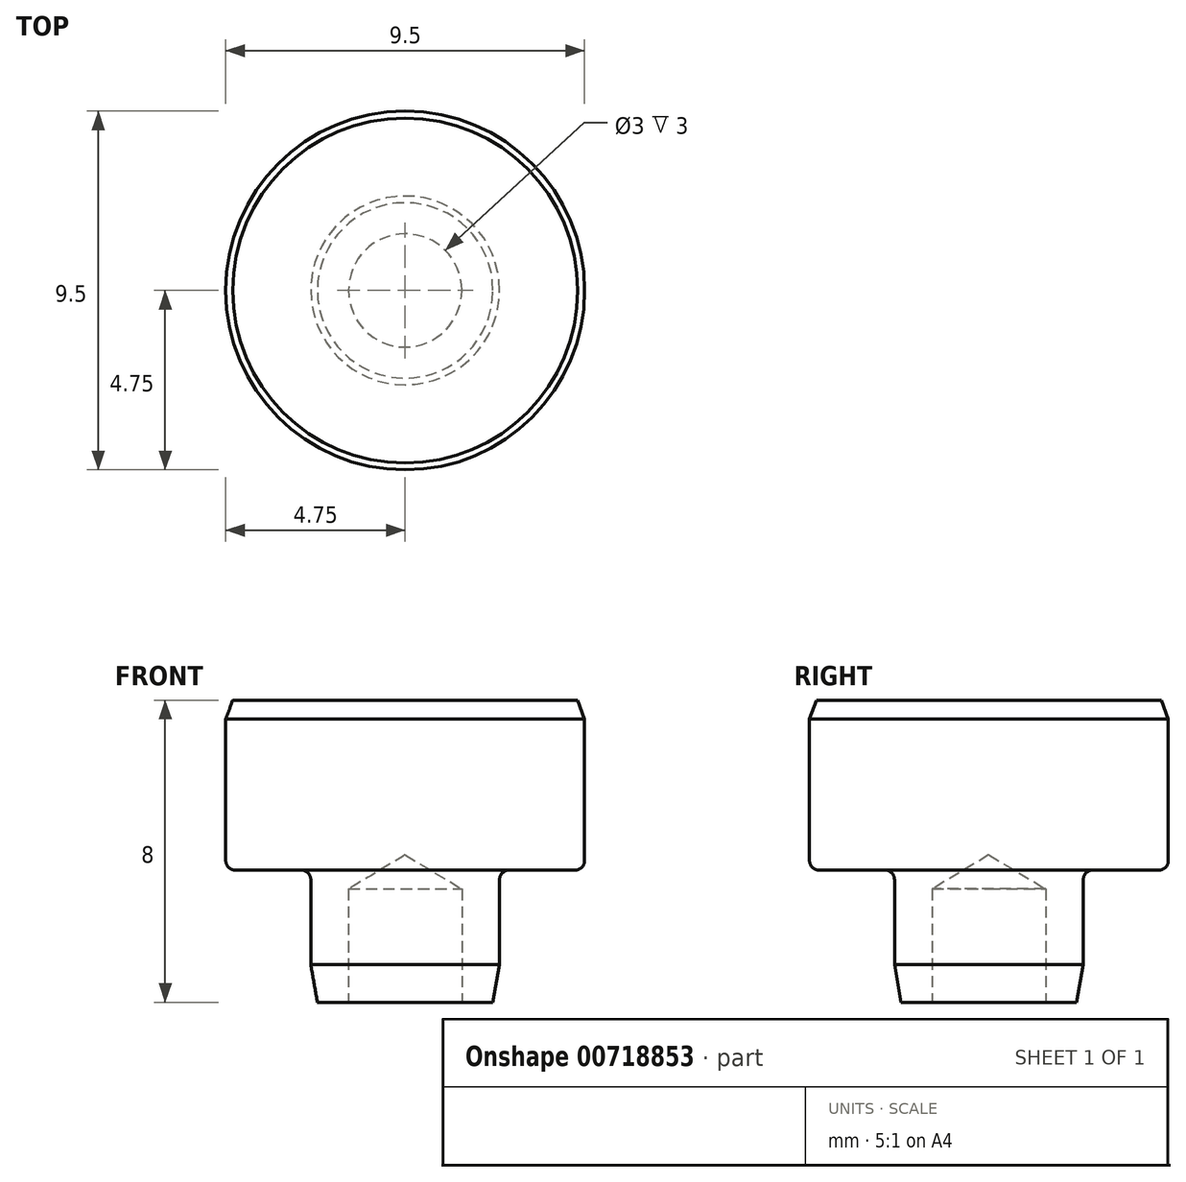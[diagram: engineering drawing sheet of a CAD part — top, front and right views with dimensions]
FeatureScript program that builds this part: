
annotation { "Feature Type Name" : "Feature", "Feature Type Description" : "" }
export const myFeature = defineFeature(function(context is Context, id is Id, definition is map)
    precondition{}
    {
        {
            var Q0;
            Q0=qCreatedBy(makeId("Right.planeOp"),FACE);
            var sketch = newSketch(context, id + "F0", { "sketchPlane" : qUnion([Q0])});
            skLineSegment(sketch, "E0.bottom", {"start": v(-4.75, 0) * mm, "end": v(0, 0) * mm});
            skLineSegment(sketch, "E0.top", {"start": v(-4.75, -4.5) * mm, "end": v(-2.5, -4.5) * mm});
            skLineSegment(sketch, "E0.left", {"start": v(-4.75, 0) * mm, "end": v(-4.75, -4.5) * mm});
            skLineSegment(sketch, "E1.top", {"start": v(-2.5, -8) * mm, "end": v(0, -8) * mm});
            skLineSegment(sketch, "E1.left", {"start": v(-2.5, -4.5) * mm, "end": v(-2.5, -8) * mm});
            skLineSegment(sketch, "E2", {"start": v(0, 0) * mm, "end": v(0, -8) * mm});
            skSolve(sketch);
        }
        {
            var Q0;
            Q0=makeQuery(id+"F0.imprint","IMPRINT",FACE,{"disambiguationData":[TD([[makeQuery(id+"F0.imprint","IMPRINT",EDGE,{"derivedFrom":sQuery(id+"F0.wireOp",EDGE,"E0.bottom")}),-1.0]])]});
            var Q1;
            Q1=sQuery(id+"F0.wireOp",EDGE,"E2");
            revolve(context, id + "F1", {"surfaceOperationType" : NewSurfaceOperationType.NEW, "entities" : qUnion([Q0]), "axis" : qUnion([Q1]), "revolveType" : RevolveType.FULL});
        }
        {
            var Q0;
            Q0=makeQuery(id+"F1.opRevolve","SWEPT_EDGE",EDGE,{"disambiguationData":[OSD([sQuery(id+"F0.wireOp",EDGE,"E0.bottom"),sQuery(id+"F0.wireOp",EDGE,"E0.left")])]});
            chamfer(context, id + "F2", {"entities" : qUnion([Q0]), "chamferType" : ChamferType.OFFSET_ANGLE, "width" : 0.5 * mm, "oppositeDirection" : true, "angle" : 20 * degree, "tangentPropagation" : true});
        }
        {
            var Q0;
            Q0=makeQuery(id+"F1.opRevolve","SWEPT_EDGE",EDGE,{"disambiguationData":[OSD([sQuery(id+"F0.wireOp",EDGE,"E0.top"),sQuery(id+"F0.wireOp",EDGE,"E0.left")])]});
            var Q1;
            Q1=makeQuery(id+"F1.opRevolve","SWEPT_EDGE",EDGE,{"disambiguationData":[OSD([sQuery(id+"F0.wireOp",EDGE,"E0.top"),sQuery(id+"F0.wireOp",EDGE,"E1.left")])]});
            fillet(context, id + "F3", {"entities" : qUnion([Q0, Q1]), "radius" : .25 * mm, "tangentPropagation" : true, "allowEdgeOverflow" : false});
        }
        {
            var Q0;
            Q0=makeQuery(id+"F1.opRevolve","SWEPT_EDGE",EDGE,{"disambiguationData":[OSD([sQuery(id+"F0.wireOp",EDGE,"E1.top"),sQuery(id+"F0.wireOp",EDGE,"E1.left")])]});
            chamfer(context, id + "F4", {"entities" : qUnion([Q0]), "chamferType" : ChamferType.OFFSET_ANGLE, "width" : 1 * mm, "oppositeDirection" : false, "angle" : 10 * degree, "tangentPropagation" : true});
        }
        {
            var Q0;
            Q0=makeQuery(id+"F1.opRevolve","SWEPT_FACE",FACE,{"disambiguationData":[OSD([sQuery(id+"F0.wireOp",EDGE,"E1.top")])]});
            var sketch = newSketch(context, id + "F5", { "sketchPlane" : qUnion([Q0])});
            skCircle(sketch, "E3", {"center": v(0, 0) * mm, "radius": 1 * mm});
            skSolve(sketch);
        }
        {
            var Q0;
            Q0=sQuery(id+"F5.wireOp",VERTEX,"E3.center");
            var Q1;
            Q1=makeQuery(id+"F1.opRevolve","SWEPT_BODY",BODY,{"disambiguationData":[OSD([sQuery(id+"F0.wireOp",EDGE,"E0.bottom"),sQuery(id+"F0.wireOp",EDGE,"E0.top"),sQuery(id+"F0.wireOp",EDGE,"E0.left"),sQuery(id+"F0.wireOp",EDGE,"E1.top"),sQuery(id+"F0.wireOp",EDGE,"E1.left"),sQuery(id+"F0.wireOp",EDGE,"E2")])]});
            hole(context, id + "F6", {"style" : HoleStyle.SIMPLE, "endStyle" : HoleEndStyle.BLIND, "holeDiameter" : 3 * mm, "majorDiameter" : 5 * mm, "holeDepth" : 3 * mm, "isTappedThrough" : true, "tappedDepth" : 12 * mm, "tapClearance" : 3, "locations" : qUnion([Q0]), "scope" : qUnion([Q1])});
        }
    });
